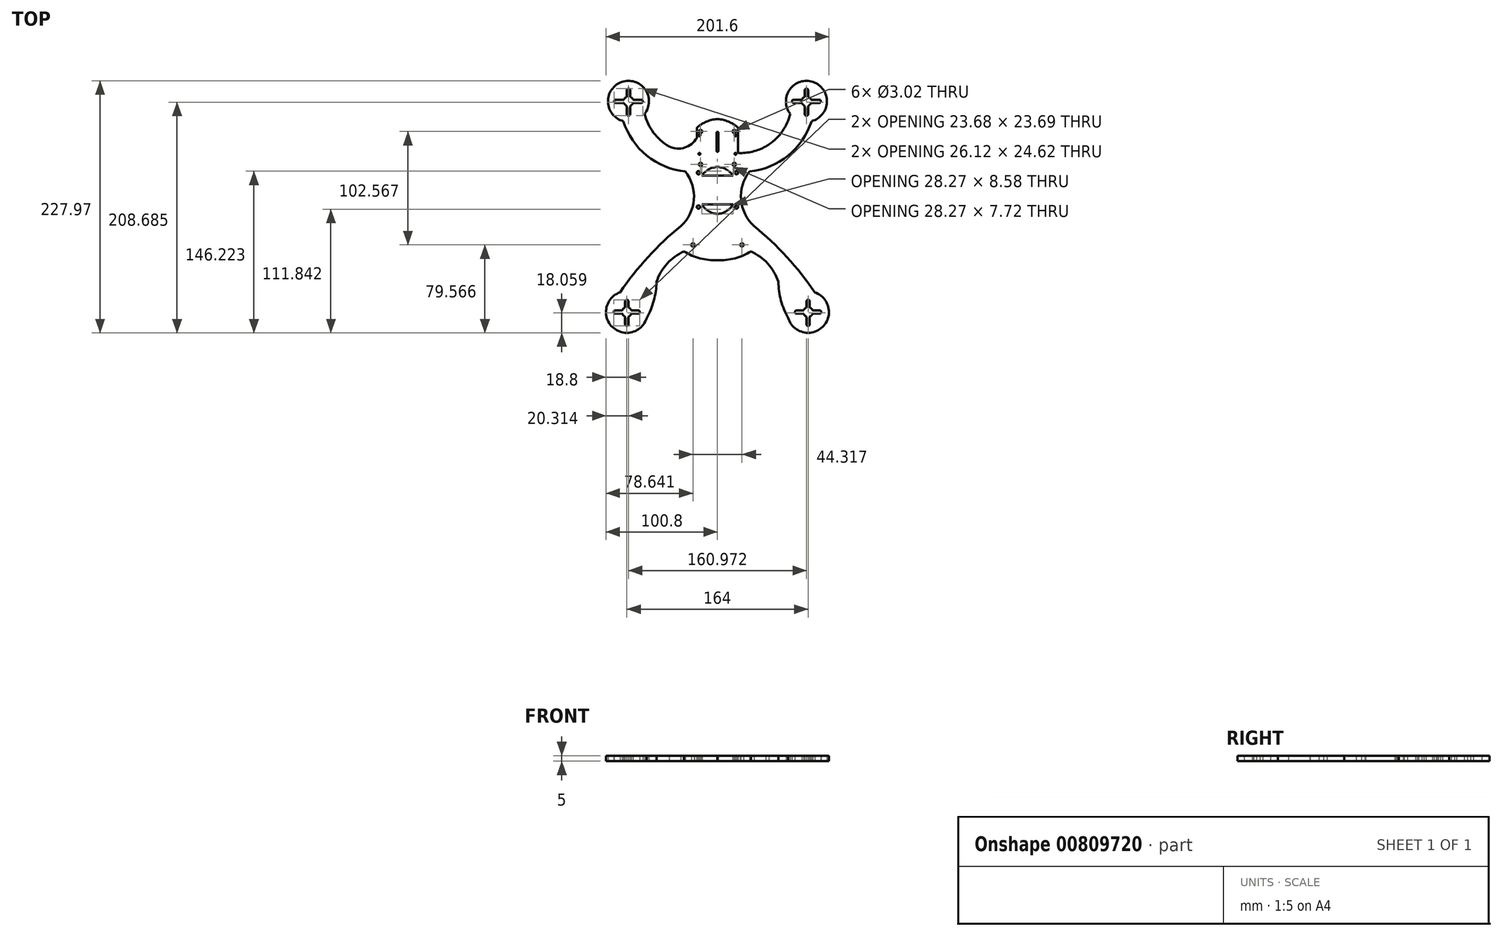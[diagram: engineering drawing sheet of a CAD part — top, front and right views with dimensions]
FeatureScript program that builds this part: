
annotation { "Feature Type Name" : "Feature", "Feature Type Description" : "" }
export const myFeature = defineFeature(function(context is Context, id is Id, definition is map)
    precondition{}
    {
        {
            var Q0;
            Q0=qCreatedBy(makeId("Top.planeOp"),FACE);
            var sketch = newSketch(context, id + "F0", { "sketchPlane" : qUnion([Q0])});
            skLineSegment(sketch, "E0", {"start": v(0, 59.62) * mm, "end": v(0, -52.38) * mm});
            skLineSegment(sketch, "E1", {"start": v(0, -52.38) * mm, "end": v(-30.19, -52.38) * mm});
            skCircle(sketch, "E2", {"center": v(-82, -107.2) * mm, "radius": 18.8 * mm});
            skCircle(sketch, "E3", {"center": v(-82, -107.2) * mm, "radius": 4.36 * mm});
            skCircle(sketch, "E4", {"center": v(-82, -118.3) * mm, "radius": 1.5 * mm});
            skCircle(sketch, "E5", {"center": v(-82, -97.6) * mm, "radius": 1.5 * mm});
            skCircle(sketch, "E6", {"center": v(-71.66, -107.2) * mm, "radius": 1.5 * mm});
            skCircle(sketch, "E7", {"center": v(-92.34, -107.2) * mm, "radius": 1.5 * mm});
            skLineSegment(sketch, "E8", {"start": v(-92.34, -108.7) * mm, "end": v(-86.1, -108.7) * mm});
            skLineSegment(sketch, "E9", {"start": v(-71.66, -108.7) * mm, "end": v(-77.9, -108.7) * mm});
            skLineSegment(sketch, "E10", {"start": v(-71.66, -105.7) * mm, "end": v(-77.9, -105.7) * mm});
            skLineSegment(sketch, "E11", {"start": v(-83.5, -118.3) * mm, "end": v(-83.5, -111.3) * mm});
            skLineSegment(sketch, "E12", {"start": v(-80.5, -118.3) * mm, "end": v(-80.5, -111.3) * mm});
            skLineSegment(sketch, "E13", {"start": v(-80.5, -97.6) * mm, "end": v(-80.5, -103.11) * mm});
            skLineSegment(sketch, "E14", {"start": v(-83.5, -97.6) * mm, "end": v(-83.5, -103.11) * mm});
            skCircle(sketch, "E15", {"center": v(-80.49, 83.43) * mm, "radius": 18.53 * mm});
            skArc(sketch, "E16", {"start": v(-64, -112.66) * mm, "mid": v(-57.49, -96.8) * mm, "end": v(-55.08, -79.81) * mm});
            skCircle(sketch, "E17", {"center": v(-80.49, 83.43) * mm, "radius": 4.36 * mm});
            skCircle(sketch, "E18", {"center": v(-80.49, 71.87) * mm, "radius": 1.5 * mm});
            skCircle(sketch, "E19", {"center": v(-68.93, 83.43) * mm, "radius": 1.5 * mm});
            skCircle(sketch, "E20", {"center": v(-92.05, 83.43) * mm, "radius": 1.5 * mm});
            skCircle(sketch, "E21", {"center": v(-80.49, 93.49) * mm, "radius": 1.5 * mm});
            skLineSegment(sketch, "E22", {"start": v(-92.05, 84.93) * mm, "end": v(-84.58, 84.93) * mm});
            skLineSegment(sketch, "E23", {"start": v(-92.05, 81.93) * mm, "end": v(-84.58, 81.93) * mm});
            skLineSegment(sketch, "E24", {"start": v(-78.99, 71.87) * mm, "end": v(-78.99, 79.33) * mm});
            skLineSegment(sketch, "E25", {"start": v(-68.93, 84.93) * mm, "end": v(-76.4, 84.93) * mm});
            skLineSegment(sketch, "E26", {"start": v(-81.99, 71.87) * mm, "end": v(-81.99, 79.33) * mm});
            skLineSegment(sketch, "E27", {"start": v(-68.93, 81.93) * mm, "end": v(-76.4, 81.93) * mm});
            skLineSegment(sketch, "E28", {"start": v(-78.99, 93.49) * mm, "end": v(-78.99, 87.52) * mm});
            skLineSegment(sketch, "E29", {"start": v(-81.99, 93.49) * mm, "end": v(-81.99, 87.52) * mm});
            skLineSegment(sketch, "E30", {"start": v(-92.34, -105.7) * mm, "end": v(-86.1, -105.7) * mm});
            skArc(sketch, "E31", {"start": v(-85.16, 65.5) * mm, "mid": v(-60.89, 32.02) * mm, "end": v(-21.44, 19.62) * mm});
            skArc(sketch, "E32", {"start": v(-20.09, -19.38) * mm, "mid": v(-57.08, -51.44) * mm, "end": v(-87.99, -89.38) * mm});
            skArc(sketch, "E33", {"start": v(-30.19, -52.38) * mm, "mid": v(-45.54, -63.46) * mm, "end": v(-55.08, -79.81) * mm});
            skArc(sketch, "E34", {"start": v(-30.19, -52.38) * mm, "mid": v(-15.7, -58.64) * mm, "end": v(0, -60.3) * mm});
            skCircle(sketch, "E35", {"center": v(-17.22, 18.8) * mm, "radius": 1.5 * mm});
            skCircle(sketch, "E36", {"center": v(-17.22, -12.2) * mm, "radius": 1.5 * mm});
            skLineSegment(sketch, "E37", {"start": v(0, 16.35) * mm, "end": v(-14.14, 16.35) * mm});
            skArc(sketch, "E38", {"start": v(0, 24.07) * mm, "mid": v(-7.95, 21.83) * mm, "end": v(-14.14, 16.35) * mm});
            skLineSegment(sketch, "E39", {"start": v(-14.14, -9.88) * mm, "end": v(0, -9.88) * mm});
            skArc(sketch, "E40", {"start": v(-14.14, -9.88) * mm, "mid": v(-8.15, -15.95) * mm, "end": v(0, -18.46) * mm});
            skCircle(sketch, "E41", {"center": v(-15.25, 26.38) * mm, "radius": 1.51 * mm});
            skCircle(sketch, "E42", {"center": v(-15.25, 56.12) * mm, "radius": 1.51 * mm});
            skLineSegment(sketch, "E43", {"start": v(-18.7, 59.62) * mm, "end": v(-18.7, 13.81) * mm});
            skArc(sketch, "E44", {"start": v(-65.76, 72.18) * mm, "mid": v(-48.67, 45.9) * mm, "end": v(-18.7, 36.71) * mm});
            skArc(sketch, "E45", {"start": v(-46.67, 44.47) * mm, "mid": v(-31.36, 41.04) * mm, "end": v(-18.7, 50.32) * mm});
            skCircle(sketch, "E46", {"center": v(-22.16, -46.44) * mm, "radius": 1.51 * mm});
            skArc(sketch, "E47", {"start": v(-33.21, -29.5) * mm, "mid": v(-21.34, -5.6) * mm, "end": v(-29.04, 19.95) * mm});
            skLineSegment(sketch, "E48", {"start": v(-21.44, 19.62) * mm, "end": v(-20.09, -19.38) * mm});
            skArc(sketch, "E49", {"start": v(0, 67.33) * mm, "mid": v(-10, 65.03) * mm, "end": v(-18.7, 59.62) * mm});
            skCircle(sketch, "E50.MirrorC", {"center": v(82, -118.3) * mm, "radius": 1.5 * mm});
            skCircle(sketch, "E51", {"center": v(-16.3, 52.75) * mm, "radius": 0.93 * mm});
            skCircle(sketch, "E52", {"center": v(0, 54.86) * mm, "radius": 0.93 * mm});
            skCircle(sketch, "E53", {"center": v(-16.3, 35.9) * mm, "radius": 0.83 * mm});
            skLineSegment(sketch, "E54", {"start": v(-17.23, 52.75) * mm, "end": v(-17.23, 35.9) * mm});
            skLineSegment(sketch, "E55", {"start": v(-15.38, 52.75) * mm, "end": v(-15.38, 35.9) * mm});
            skCircle(sketch, "E56.MirrorC", {"center": v(16.3, 52.75) * mm, "radius": 0.93 * mm});
            skLineSegment(sketch, "E57.MirrorCS", {"start": v(92.34, -105.7) * mm, "end": v(86.1, -105.7) * mm});
            skLineSegment(sketch, "E58.MirrorCS", {"start": v(80.5, -118.3) * mm, "end": v(80.5, -111.3) * mm});
            skLineSegment(sketch, "E59.MirrorCS", {"start": v(83.5, -97.6) * mm, "end": v(83.5, -103.11) * mm});
            skCircle(sketch, "E60.MirrorC", {"center": v(80.49, 83.43) * mm, "radius": 4.36 * mm});
            skLineSegment(sketch, "E61.MirrorCS", {"start": v(80.5, -97.6) * mm, "end": v(80.5, -103.11) * mm});
            skCircle(sketch, "E62.MirrorC", {"center": v(68.93, 83.43) * mm, "radius": 1.5 * mm});
            skLineSegment(sketch, "E63.MirrorCS", {"start": v(68.93, 84.93) * mm, "end": v(76.4, 84.93) * mm});
            skLineSegment(sketch, "E64.MirrorCS", {"start": v(71.66, -105.7) * mm, "end": v(77.9, -105.7) * mm});
            skLineSegment(sketch, "E65.MirrorCS", {"start": v(83.5, -118.3) * mm, "end": v(83.5, -111.3) * mm});
            skCircle(sketch, "E66.MirrorC", {"center": v(82, -97.6) * mm, "radius": 1.5 * mm});
            skCircle(sketch, "E67.MirrorC", {"center": v(82, -107.2) * mm, "radius": 4.36 * mm});
            skLineSegment(sketch, "E68.MirrorCS", {"start": v(68.93, 81.93) * mm, "end": v(76.4, 81.93) * mm});
            skCircle(sketch, "E69.MirrorC", {"center": v(16.3, 35.9) * mm, "radius": 0.83 * mm});
            skCircle(sketch, "E70.MirrorC", {"center": v(92.34, -107.2) * mm, "radius": 1.5 * mm});
            skCircle(sketch, "E71.MirrorC", {"center": v(15.25, 26.38) * mm, "radius": 1.51 * mm});
            skLineSegment(sketch, "E72.MirrorCS", {"start": v(81.99, 71.87) * mm, "end": v(81.99, 79.33) * mm});
            skCircle(sketch, "E73.MirrorC", {"center": v(15.25, 56.12) * mm, "radius": 1.51 * mm});
            skLineSegment(sketch, "E74.MirrorCS", {"start": v(92.05, 84.93) * mm, "end": v(84.58, 84.93) * mm});
            skCircle(sketch, "E75.MirrorC", {"center": v(92.05, 83.43) * mm, "radius": 1.5 * mm});
            skLineSegment(sketch, "E76.MirrorCS", {"start": v(78.99, 71.87) * mm, "end": v(78.99, 79.33) * mm});
            skLineSegment(sketch, "E77.MirrorCS", {"start": v(78.99, 93.49) * mm, "end": v(78.99, 87.52) * mm});
            skLineSegment(sketch, "E78.MirrorCS", {"start": v(81.99, 93.49) * mm, "end": v(81.99, 87.52) * mm});
            skCircle(sketch, "E79.MirrorC", {"center": v(80.49, 93.49) * mm, "radius": 1.5 * mm});
            skCircle(sketch, "E80.MirrorC", {"center": v(17.22, 18.8) * mm, "radius": 1.5 * mm});
            skCircle(sketch, "E81.MirrorC", {"center": v(80.49, 71.87) * mm, "radius": 1.5 * mm});
            skLineSegment(sketch, "E82.MirrorCS", {"start": v(92.34, -108.7) * mm, "end": v(86.1, -108.7) * mm});
            skCircle(sketch, "E83.MirrorC", {"center": v(17.22, -12.2) * mm, "radius": 1.5 * mm});
            skLineSegment(sketch, "E84.MirrorCS", {"start": v(71.66, -108.7) * mm, "end": v(77.9, -108.7) * mm});
            skLineSegment(sketch, "E85.MirrorCS", {"start": v(92.05, 81.93) * mm, "end": v(84.58, 81.93) * mm});
            skCircle(sketch, "E86.MirrorC", {"center": v(71.66, -107.2) * mm, "radius": 1.5 * mm});
            skLineSegment(sketch, "E87.MirrorCS", {"start": v(14.14, -9.88) * mm, "end": v(0, -9.88) * mm});
            skLineSegment(sketch, "E88.MirrorCS", {"start": v(17.23, 52.75) * mm, "end": v(17.23, 35.9) * mm});
            skCircle(sketch, "E89.MirrorC", {"center": v(22.16, -46.44) * mm, "radius": 1.51 * mm});
            skArc(sketch, "E90.MirrorCS", {"start": v(14.14, -9.88) * mm, "mid": v(8.15, -15.95) * mm, "end": v(0, -18.46) * mm});
            skArc(sketch, "E91.MirrorCS", {"start": v(0, 24.07) * mm, "mid": v(7.95, 21.83) * mm, "end": v(14.14, 16.35) * mm});
            skCircle(sketch, "E92.MirrorC", {"center": v(80.49, 83.43) * mm, "radius": 18.53 * mm});
            skLineSegment(sketch, "E93.MirrorCS", {"start": v(21.44, 19.62) * mm, "end": v(20.09, -19.38) * mm});
            skArc(sketch, "E94.MirrorCS", {"start": v(30.19, -52.38) * mm, "mid": v(45.54, -63.46) * mm, "end": v(55.08, -79.81) * mm});
            skArc(sketch, "E95.MirrorCS", {"start": v(0, 67.33) * mm, "mid": v(10, 65.03) * mm, "end": v(18.7, 59.62) * mm});
            skLineSegment(sketch, "E96.MirrorCS", {"start": v(0, -52.38) * mm, "end": v(30.19, -52.38) * mm});
            skArc(sketch, "E97.MirrorCS", {"start": v(65.76, 72.18) * mm, "mid": v(48.67, 45.9) * mm, "end": v(18.7, 36.71) * mm});
            skLineSegment(sketch, "E98.MirrorCS", {"start": v(15.38, 52.75) * mm, "end": v(15.38, 35.9) * mm});
            skCircle(sketch, "E99.MirrorC", {"center": v(82, -107.2) * mm, "radius": 18.8 * mm});
            skArc(sketch, "E100.MirrorCS", {"start": v(20.09, -19.38) * mm, "mid": v(57.08, -51.44) * mm, "end": v(87.99, -89.38) * mm});
            skArc(sketch, "E101.MirrorCS", {"start": v(85.16, 65.5) * mm, "mid": v(60.89, 32.02) * mm, "end": v(21.44, 19.62) * mm});
            skLineSegment(sketch, "E102.MirrorCS", {"start": v(0, 16.35) * mm, "end": v(14.14, 16.35) * mm});
            skArc(sketch, "E103.MirrorCS", {"start": v(46.67, 44.47) * mm, "mid": v(31.36, 41.04) * mm, "end": v(18.7, 50.32) * mm});
            skLineSegment(sketch, "E104.MirrorCS", {"start": v(18.7, 59.62) * mm, "end": v(18.7, 13.81) * mm});
            skArc(sketch, "E105.MirrorCS", {"start": v(30.19, -52.38) * mm, "mid": v(15.7, -58.64) * mm, "end": v(0, -60.3) * mm});
            skArc(sketch, "E106.MirrorCS", {"start": v(64, -112.66) * mm, "mid": v(57.49, -96.8) * mm, "end": v(55.08, -79.81) * mm});
            skArc(sketch, "E107.MirrorCS", {"start": v(33.21, -29.5) * mm, "mid": v(21.34, -5.6) * mm, "end": v(29.04, 19.95) * mm});
            skLineSegment(sketch, "E108", {"start": v(0, 54.86) * mm, "end": v(0, 39.75) * mm});
            skCircle(sketch, "E109", {"center": v(0, 38.7) * mm, "radius": 0.93 * mm});
            skLineSegment(sketch, "E110", {"start": v(-0.93, 54.86) * mm, "end": v(-0.93, 38.7) * mm});
            skLineSegment(sketch, "E111", {"start": v(0.93, 54.86) * mm, "end": v(0.93, 38.7) * mm});
            skLineSegment(sketch, "E112", {"start": v(-82, -126) * mm, "end": v(-127.24, -126) * mm});
            skLineSegment(sketch, "E113", {"start": v(-80.49, 101.96) * mm, "end": v(-140.03, 101.96) * mm});
            skLineSegment(sketch, "E114", {"start": v(-124.72, 101.96) * mm, "end": v(-124.72, -126) * mm});
            skSolve(sketch);
        }
        {
            var Q0;
            Q0=makeQuery(id+"F0.imprint","IMPRINT",FACE,{"disambiguationData":[TD([[makeQuery(id+"F0.imprint","IMPRINT",EDGE,{"derivedFrom":sQuery(id+"F0.wireOp",EDGE,"E1")}),1.0]])]});
            var Q1;
            {var subQ2=sQuery(id+"F0.wireOp",EDGE,"E47");Q1=makeQuery(id+"F0.imprint","IMPRINT",FACE,{"disambiguationData":[TD([[makeQuery(id+"F0.imprint","IMPRINT",EDGE,{"derivedFrom":subQ2}),-1.0]])]});}
            var Q2;
            {var subQ0=sQuery(id+"F0.wireOp",EDGE,"E44");var subQ1=sQuery(id+"F0.wireOp",EDGE,"E43");var subQ2=makeQuery(id+"F0.imprint","INTERSECT",VERTEX,{"derivedFrom":[subQ1,subQ0]});Q2=makeQuery(id+"F0.imprint","IMPRINT",FACE,{"disambiguationData":[TD([[makeQuery(id+"F0.imprint","IMPRINT",EDGE,{"disambiguationData":[TD([[subQ2,1.0]])],"derivedFrom":subQ1}),-1.0]])]});}
            var Q3;
            {var subQ0=sQuery(id+"F0.wireOp",EDGE,"E45");var subQ1=sQuery(id+"F0.wireOp",EDGE,"E44");var subQ2=makeQuery(id+"F0.imprint","INTERSECT",VERTEX,{"disambiguationData":[OD(0.0)],"derivedFrom":[subQ1,subQ0]});Q3=makeQuery(id+"F0.imprint","IMPRINT",FACE,{"disambiguationData":[TD([[makeQuery(id+"F0.imprint","IMPRINT",EDGE,{"disambiguationData":[TD([[subQ2,-1.0]])],"derivedFrom":subQ1}),-1.0]])]});}
            var Q4;
            Q4=makeQuery(id+"F0.imprint","IMPRINT",FACE,{"disambiguationData":[TD([[makeQuery(id+"F0.imprint","IMPRINT",EDGE,{"derivedFrom":sQuery(id+"F0.wireOp",EDGE,"1970e8cf-01bf-4d2f-893a-c7edce89ae3a28.MirrorC")}),-1.0]])]});
            var Q5;
            {var subQ0=sQuery(id+"F0.wireOp",EDGE,"1970e8cf-01bf-4d2f-893a-c7edce89ae3a36.MirrorCS");Q5=makeQuery(id+"F0.imprint","IMPRINT",FACE,{"disambiguationData":[TD([[makeQuery(id+"F0.imprint","IMPRINT",EDGE,{"derivedFrom":subQ0}),1.0]])]});}
            var Q6;
            {var subQ0=sQuery(id+"F0.wireOp",EDGE,"1970e8cf-01bf-4d2f-893a-c7edce89ae3a47.MirrorCS");var subQ1=sQuery(id+"F0.wireOp",EDGE,"1970e8cf-01bf-4d2f-893a-c7edce89ae3a38.MirrorCS");var subQ2=makeQuery(id+"F0.imprint","INTERSECT",VERTEX,{"disambiguationData":[OD(0.0)],"derivedFrom":[subQ1,subQ0]});Q6=makeQuery(id+"F0.imprint","IMPRINT",FACE,{"disambiguationData":[TD([[makeQuery(id+"F0.imprint","IMPRINT",EDGE,{"disambiguationData":[TD([[subQ2,-1.0]])],"derivedFrom":subQ1}),1.0]])]});}
            var Q7;
            {var subQ0=sQuery(id+"F0.wireOp",EDGE,"1970e8cf-01bf-4d2f-893a-c7edce89ae3a46.MirrorCS");var subQ1=sQuery(id+"F0.wireOp",EDGE,"1970e8cf-01bf-4d2f-893a-c7edce89ae3a38.MirrorCS");var subQ2=makeQuery(id+"F0.imprint","INTERSECT",VERTEX,{"derivedFrom":[subQ1,subQ0]});Q7=makeQuery(id+"F0.imprint","IMPRINT",FACE,{"disambiguationData":[TD([[makeQuery(id+"F0.imprint","IMPRINT",EDGE,{"disambiguationData":[TD([[subQ2,1.0]])],"derivedFrom":subQ1}),-1.0]])]});}
            var Q8;
            {var subQ2=sQuery(id+"F0.wireOp",EDGE,"1970e8cf-01bf-4d2f-893a-c7edce89ae3a24.MirrorCS");Q8=makeQuery(id+"F0.imprint","IMPRINT",FACE,{"disambiguationData":[TD([[makeQuery(id+"F0.imprint","IMPRINT",EDGE,{"derivedFrom":subQ2}),-1.0]])]});}
            var Q9;
            {var subQ0=sQuery(id+"F0.wireOp",EDGE,"E43");var subQ1=sQuery(id+"F0.wireOp",EDGE,"E35");var subQ2=makeQuery(id+"F0.imprint","INTERSECT",VERTEX,{"disambiguationData":[OD(0.0)],"derivedFrom":[subQ1,subQ0]});Q9=makeQuery(id+"F0.imprint","IMPRINT",FACE,{"disambiguationData":[TD([[makeQuery(id+"F0.imprint","IMPRINT",EDGE,{"disambiguationData":[TD([[subQ2,1.0]])],"derivedFrom":subQ1}),1.0]])]});}
            var Q10;
            {var subQ0=sQuery(id+"F0.wireOp",EDGE,"1970e8cf-01bf-4d2f-893a-c7edce89ae3a46.MirrorCS");var subQ1=sQuery(id+"F0.wireOp",EDGE,"1970e8cf-01bf-4d2f-893a-c7edce89ae3a11.MirrorC");var subQ2=makeQuery(id+"F0.imprint","INTERSECT",VERTEX,{"disambiguationData":[OD(0.0)],"derivedFrom":[subQ1,subQ0]});Q10=makeQuery(id+"F0.imprint","IMPRINT",FACE,{"disambiguationData":[TD([[makeQuery(id+"F0.imprint","IMPRINT",EDGE,{"disambiguationData":[TD([[subQ2,1.0]])],"derivedFrom":subQ1}),-1.0]])]});}
            var Q11;
            {var subQ0=sQuery(id+"F0.wireOp",EDGE,"E8");Q11=makeQuery(id+"F0.imprint","IMPRINT",FACE,{"disambiguationData":[TD([[makeQuery(id+"F0.imprint","IMPRINT",EDGE,{"derivedFrom":subQ0}),-1.0]])]});}
            var Q12;
            {var subQ3=sQuery(id+"F0.wireOp",EDGE,"E22");Q12=makeQuery(id+"F0.imprint","IMPRINT",FACE,{"disambiguationData":[TD([[makeQuery(id+"F0.imprint","IMPRINT",EDGE,{"derivedFrom":subQ3}),1.0]])]});}
            var Q13;
            {var subQ13=sQuery(id+"F0.wireOp",EDGE,"1970e8cf-01bf-4d2f-893a-c7edce89ae3a8.MirrorCS");Q13=makeQuery(id+"F0.imprint","IMPRINT",FACE,{"disambiguationData":[TD([[makeQuery(id+"F0.imprint","IMPRINT",EDGE,{"derivedFrom":subQ13}),1.0]])]});}
            var Q14;
            {var subQ2=sQuery(id+"F0.wireOp",EDGE,"1970e8cf-01bf-4d2f-893a-c7edce89ae3a1.MirrorCS");Q14=makeQuery(id+"F0.imprint","IMPRINT",FACE,{"disambiguationData":[TD([[makeQuery(id+"F0.imprint","IMPRINT",EDGE,{"derivedFrom":subQ2}),-1.0]])]});}
            var Q15;
            {var subQ1=sQuery(id+"F0.wireOp",EDGE,"71e4ceb2-40d3-4ac1-b8c6-fa41186b85900.MirrorCS");Q15=makeQuery(id+"F0.imprint","IMPRINT",FACE,{"disambiguationData":[TD([[makeQuery(id+"F0.imprint","IMPRINT",EDGE,{"derivedFrom":subQ1}),1.0]])]});}
            var Q16;
            {var subQ3=sQuery(id+"F0.wireOp",EDGE,"71e4ceb2-40d3-4ac1-b8c6-fa41186b85902.MirrorCS");Q16=makeQuery(id+"F0.imprint","IMPRINT",FACE,{"disambiguationData":[TD([[makeQuery(id+"F0.imprint","IMPRINT",EDGE,{"derivedFrom":subQ3}),-1.0]])]});}
            var Q17;
            {var subQ0=sQuery(id+"F0.wireOp",EDGE,"71e4ceb2-40d3-4ac1-b8c6-fa41186b859038.MirrorCS");var subQ1=sQuery(id+"F0.wireOp",EDGE,"71e4ceb2-40d3-4ac1-b8c6-fa41186b859036.MirrorCS");var subQ2=makeQuery(id+"F0.imprint","INTERSECT",VERTEX,{"derivedFrom":[subQ1,subQ0]});Q17=makeQuery(id+"F0.imprint","IMPRINT",FACE,{"disambiguationData":[TD([[makeQuery(id+"F0.imprint","IMPRINT",EDGE,{"disambiguationData":[TD([[subQ2,-1.0]])],"derivedFrom":subQ1}),1.0]])]});}
            var Q18;
            {var subQ0=sQuery(id+"F0.wireOp",EDGE,"71e4ceb2-40d3-4ac1-b8c6-fa41186b859045.MirrorCS");Q18=makeQuery(id+"F0.imprint","IMPRINT",FACE,{"disambiguationData":[TD([[makeQuery(id+"F0.imprint","IMPRINT",EDGE,{"derivedFrom":subQ0}),1.0]])]});}
            var Q19;
            {var subQ3=sQuery(id+"F0.wireOp",EDGE,"E63.MirrorCS");Q19=makeQuery(id+"F0.imprint","IMPRINT",FACE,{"disambiguationData":[TD([[makeQuery(id+"F0.imprint","IMPRINT",EDGE,{"derivedFrom":subQ3}),1.0]])]});}
            var Q20;
            {var subQ8=sQuery(id+"F0.wireOp",EDGE,"E57.MirrorCS");Q20=makeQuery(id+"F0.imprint","IMPRINT",FACE,{"disambiguationData":[TD([[makeQuery(id+"F0.imprint","IMPRINT",EDGE,{"derivedFrom":subQ8}),-1.0]])]});}
            var Q21;
            Q21=makeQuery(id+"F0.imprint","IMPRINT",FACE,{"disambiguationData":[TD([[makeQuery(id+"F0.imprint","IMPRINT",EDGE,{"derivedFrom":sQuery(id+"F0.wireOp",EDGE,"E1")}),-1.0]])]});
            var Q22;
            {var subQ0=sQuery(id+"F0.wireOp",EDGE,"E104.MirrorCS");var subQ1=sQuery(id+"F0.wireOp",EDGE,"E97.MirrorCS");var subQ2=makeQuery(id+"F0.imprint","INTERSECT",VERTEX,{"derivedFrom":[subQ1,subQ0]});Q22=makeQuery(id+"F0.imprint","IMPRINT",FACE,{"disambiguationData":[TD([[makeQuery(id+"F0.imprint","IMPRINT",EDGE,{"disambiguationData":[TD([[subQ2,1.0]])],"derivedFrom":subQ1}),-1.0]])]});}
            var Q23;
            {var subQ0=sQuery(id+"F0.wireOp",EDGE,"E93.MirrorCS");Q23=makeQuery(id+"F0.imprint","IMPRINT",FACE,{"disambiguationData":[TD([[makeQuery(id+"F0.imprint","IMPRINT",EDGE,{"derivedFrom":subQ0}),1.0]])]});}
            extrude(context, id + "F1", {"entities" : qUnion([Q0, Q1, Q2, Q3, Q4, Q5, Q6, Q7, Q8, Q9, Q10, Q11, Q12, Q13, Q14, Q15, Q16, Q17, Q18, Q19, Q20, Q21, Q22, Q23]), "endBound" : BoundingType.SYMMETRIC, "depth" : 5 * mm, "offsetDistance" : 25 * mm});
        }
    });
